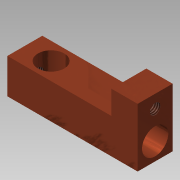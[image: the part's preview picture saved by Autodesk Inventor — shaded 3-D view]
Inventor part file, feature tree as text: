
AUTODESK INVENTOR PART (.ipt)
format: ipt  version: 2014 (Build 180170000, 170)  size: 140,800 bytes
history: native  units: mm
features: extrude x5, sketch x5, thread x2, reference x1
ambient origin geometry x8: Origin, YZ Plane, XZ Plane, XY Plane, X Axis, Y Axis, Z Axis, Center Point
bodies: Solid1 (feature_tree)
feature tree (13):
  extrude  "Extrusion1"  Depth=8.0mm
  extrude  "Extrusion2"  Depth=8.0mm TaperAngle=0.0deg
  extrude  "Extrusion3"  Depth=19.8mm TaperAngle=0.0deg
  thread  "Thread1"  [1 undecoded]
  extrude  "Extrusion5"  Depth=10.0mm TaperAngle=0.0deg
  extrude  "Extrusion6"  Depth=5.4mm TaperAngle=0.0deg
  thread  "Thread3"  [1 undecoded]
  sketch  "Sketch1"  dims[d0=12.0mm d1=8.0mm]
  reference  "Reference1"
  sketch  "Sketch2"  dims[d2=17.8mm d3=8.0mm d4=0.0mm]
  sketch  "Sketch3"  dims[d5=6.0mm d6=19.8mm d7=0.0mm d8=2.4mm]
  sketch  "Sketch5"  dims[d9=4.0mm d10=0.0mm d11=10.0mm d12=0.0mm]
  sketch  "Sketch6"  dims[d20=6.0mm d21=5.4mm d22=0.0mm d23=2.4mm d24=3.0mm d25=10.0mm d26=0.0mm d27=10.0mm d28=0.0mm]
note: 2 required parameter values undecoded (feature->parameter linkage not recoverable at this tier; creation-order binding heuristic only, values carry confidence <= 0.55)
